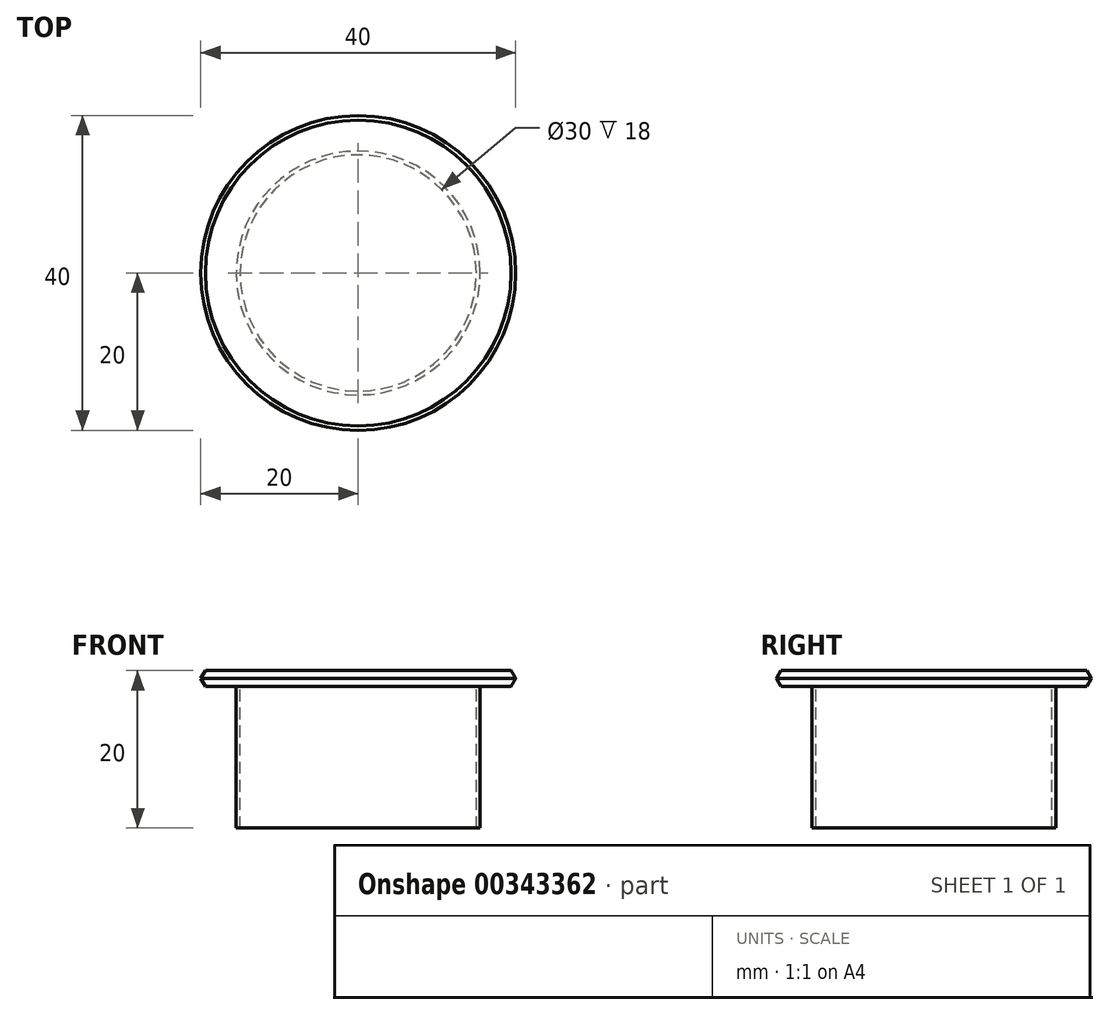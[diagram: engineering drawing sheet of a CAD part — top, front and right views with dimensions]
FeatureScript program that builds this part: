
annotation { "Feature Type Name" : "Feature", "Feature Type Description" : "" }
export const myFeature = defineFeature(function(context is Context, id is Id, definition is map)
    precondition{}
    {
        {
            var Q0;
            Q0=qCreatedBy(makeId("Top.planeOp"),FACE);
            var sketch = newSketch(context, id + "F0", { "sketchPlane" : qUnion([Q0])});
            skCircle(sketch, "E0", {"center": v(0, 0) * mm, "radius": 20 * mm});
            skSolve(sketch);
        }
        {
            var Q0;
            Q0=qSketchRegion(id+"F0",true);
            extrude(context, id + "F1", {"entities" : qUnion([Q0]), "depth" : 1 * mm, "hasDraft" : true, "draftAngle" : 30 * degree, "draftPullDirection" : true, "hasSecondDirection" : true, "secondDirectionOppositeDirection" : true, "secondDirectionDepth" : 1 * mm, "hasSecondDirectionDraft" : true, "secondDirectionDraftAngle" : 30 * degree, "secondDirectionDraftPullDirection" : true});
        }
        {
            var Q0;
            Q0=makeQuery(id+"F1.opExtrude","CAP_FACE",FACE,{"disambiguationData":[OSD([sQuery(id+"F0.wireOp",EDGE,"E0")])],"isStart":true});
            var sketch = newSketch(context, id + "F2", { "sketchPlane" : qUnion([Q0])});
            skCircle(sketch, "E1", {"center": v(0, 0) * mm, "radius": 15 * mm});
            skCircle(sketch, "E2", {"center": v(0, 0) * mm, "radius": 15.5 * mm});
            skSolve(sketch);
        }
        {
            var Q0;
            Q0=qSketchRegion(id+"F2",true);
            extrude(context, id + "F3", {"entities" : qUnion([Q0]), "operationType" : NewBodyOperationType.ADD, "depth" : 18 * mm});
        }
    });
